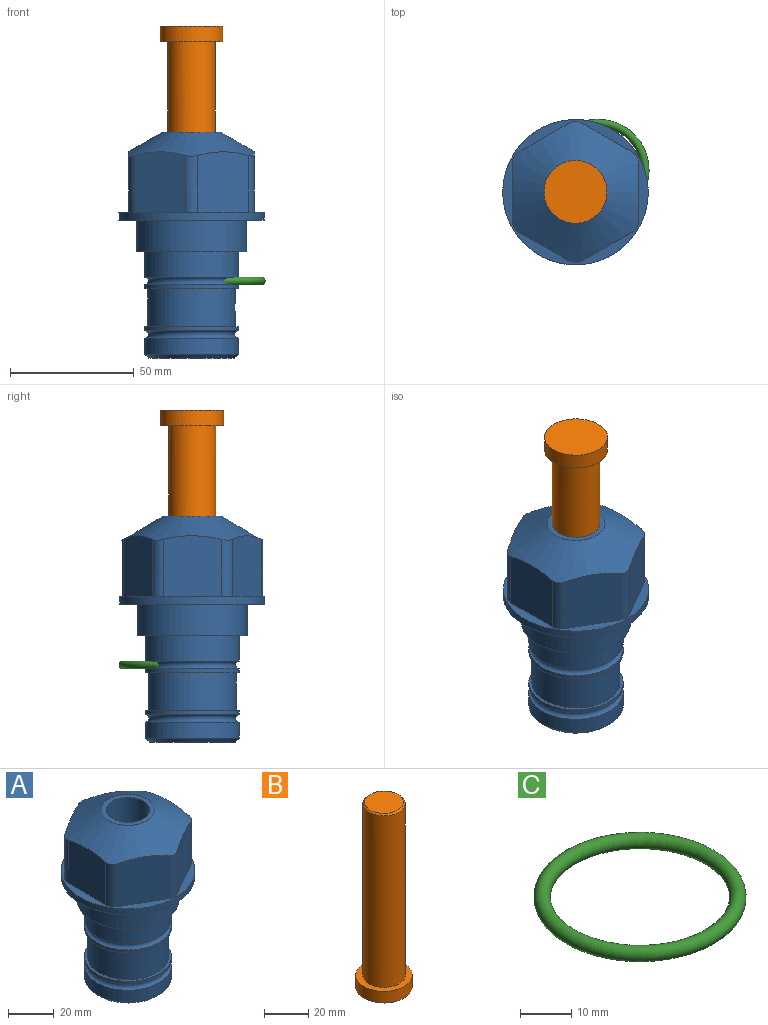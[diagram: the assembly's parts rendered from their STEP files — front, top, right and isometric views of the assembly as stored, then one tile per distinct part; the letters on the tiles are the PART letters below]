
ASSEMBLY  parts=3 mates=1
PART A: 36 faces, bbox 58.7x58.7x91.2 mm
  f0: cylinder r=17.78mm len=35.56mm, axis (0,0,1), area 1670.8mm2, adj f23,f24,f31
  f1: cylinder r=19.05mm len=38.1mm, axis (0,0,1), area 1191.9mm2, adj f26,f27,f30
  f2: plane 58.66x58.66mm, normal (0,0,-1), area 1150.6mm2, adj f3,f28
  f3: cylinder r=29.33mm len=58.66mm, axis (0,0,-1), area 585.1mm2, adj f2,f4
  f4: plane 58.66x58.66mm, normal (0,0,1), area 475.9mm2, adj f3,f5,f6,f7,f8,f9,f10,f11
  f5: plane 24.5x20.32mm, normal (-0.5,0.87,0), area 562.8mm2, adj f4,f15,f16,f17
  f6: plane 24.5x20.32mm, normal (0.5,0.87,0), area 562.8mm2, adj f4,f14,f15,f17
  f7: plane 24.5x23.48mm, normal (1,0,0), area 562.8mm2, adj f4,f13,f14,f17
  f8: plane 24.5x20.32mm, normal (0.5,-0.87,0), area 562.8mm2, adj f4,f12,f13,f17
  f9: plane 24.5x20.32mm, normal (-0.5,-0.87,0), area 562.8mm2, adj f4,f11,f12,f17
  f10: plane 24.5x23.48mm, normal (-1,0,0), area 562.8mm2, adj f4,f11,f16,f17
  f11: cylinder r=5.08mm len=23.01mm, axis (0,0,-1), area 121.2mm2, adj f4,f9,f10,f17
  f12: cylinder r=5.08mm len=23.01mm, axis (0,0,-1), area 121.2mm2, adj f4,f8,f9,f17
  f13: cylinder r=5.08mm len=23.01mm, axis (0,0,-1), area 121.2mm2, adj f4,f7,f8,f17
  f14: cylinder r=5.08mm len=23.01mm, axis (0,0,-1), area 121.2mm2, adj f4,f6,f7,f17
  f15: cylinder r=5.08mm len=23.01mm, axis (0,0,-1), area 121.2mm2, adj f4,f5,f6,f17
  f16: cylinder r=5.08mm len=23.01mm, axis (0,0,-1), area 121.2mm2, adj f4,f5,f10,f17
  f17: cone r=11.73mm half-angle=60deg, axis (0,0,-1), area 2071.8mm2, adj f5,f6,f7,f8,f9,f10,f11,f12
  f18: plane 23.46x23.46mm, normal (0,0,1), area 147.4mm2, adj f17,f35
  f19: plane 34.93x34.93mm, normal (0,0,-1), area 958mm2, adj f29
  f20: cylinder r=19.05mm len=38.1mm, axis (0,0,1), area 760.1mm2, adj f21,f29
  f21: torus R=19.05mm, axis (0,0,1), area 565.3mm2, adj f20,f22
  f22: cylinder r=19.05mm len=38.1mm, axis (0,0,1), area 190mm2, adj f21,f23
  f23: plane 38.1x38.1mm, normal (0,0,1), area 146.9mm2, adj f0,f22
  f24: plane 38.1x38.1mm, normal (0,0,-1), area 146.9mm2, adj f0,f25
  f25: cylinder r=19.05mm len=38.1mm, axis (0,0,1), area 190mm2, adj f24,f26
  f26: torus R=19.05mm, axis (0,0,1), area 565.3mm2, adj f1,f25
  f27: plane 44.45x44.45mm, normal (0,0,-1), area 411.7mm2, adj f1,f28
  f28: cylinder r=22.23mm len=44.45mm, axis (0,0,1), area 1773.5mm2, adj f2,f27
  f29: cone r=19.05mm half-angle=45deg, axis (0,0,1), area 257.5mm2, adj f19,f20
  f30: cylinder r=3.17mm len=6.75mm, axis (-1,0,0), area 128mm2, adj f1,f33
  f31: cylinder r=3.17mm len=6.35mm, axis (-1,0,0), area 102.5mm2, adj f0,f33
  f32: plane 25.4x25.4mm, normal (0,0,1), area 506.7mm2, adj f33
  f33: cylinder r=12.7mm len=66.42mm, axis (0,0,-1), area 5236.2mm2, adj f30,f31,f32,f34
  f34: cone r=9.53mm half-angle=30deg, axis (0,0,-1), area 443.4mm2, adj f33,f35
  f35: cylinder r=9.53mm len=19.05mm, axis (0,0,-1), area 849mm2, adj f18,f34
PART B: 6 faces, bbox 25.4x25.4x101.6 mm
  f0: plane 17.46x17.46mm, normal (0,0,1), area 239.5mm2, adj f5
  f1: plane 25.4x25.4mm, normal (0,0,-1), area 506.7mm2, adj f2
  f2: cylinder r=12.7mm len=25.4mm, axis (0,0,1), area 506.7mm2, adj f1,f3
  f3: plane 25.4x25.4mm, normal (0,0,1), area 221.7mm2, adj f2,f4
  f4: cylinder r=9.53mm len=94.46mm, axis (0,0,1), area 5653mm2, adj f3,f5
  f5: cone r=8.73mm half-angle=45deg, axis (0,0,-1), area 64.4mm2, adj f0,f4
PART C: 1 faces, bbox 44.7x44.7x3.2 mm
  f0: torus R=19.05mm, axis (0,0,1), area 1193.9mm2
PLACE A t=(-9.07,-8.9,0)mm
PLACE B rot(axis=(1,0,0),180deg) t=(-9.07,-8.9,50.49)mm
PLACE C at identity
MATE cylindrical B.f2 <-> A.f0  axis (0,0,-1) through (-9.07,-8.9,24.85)mm
